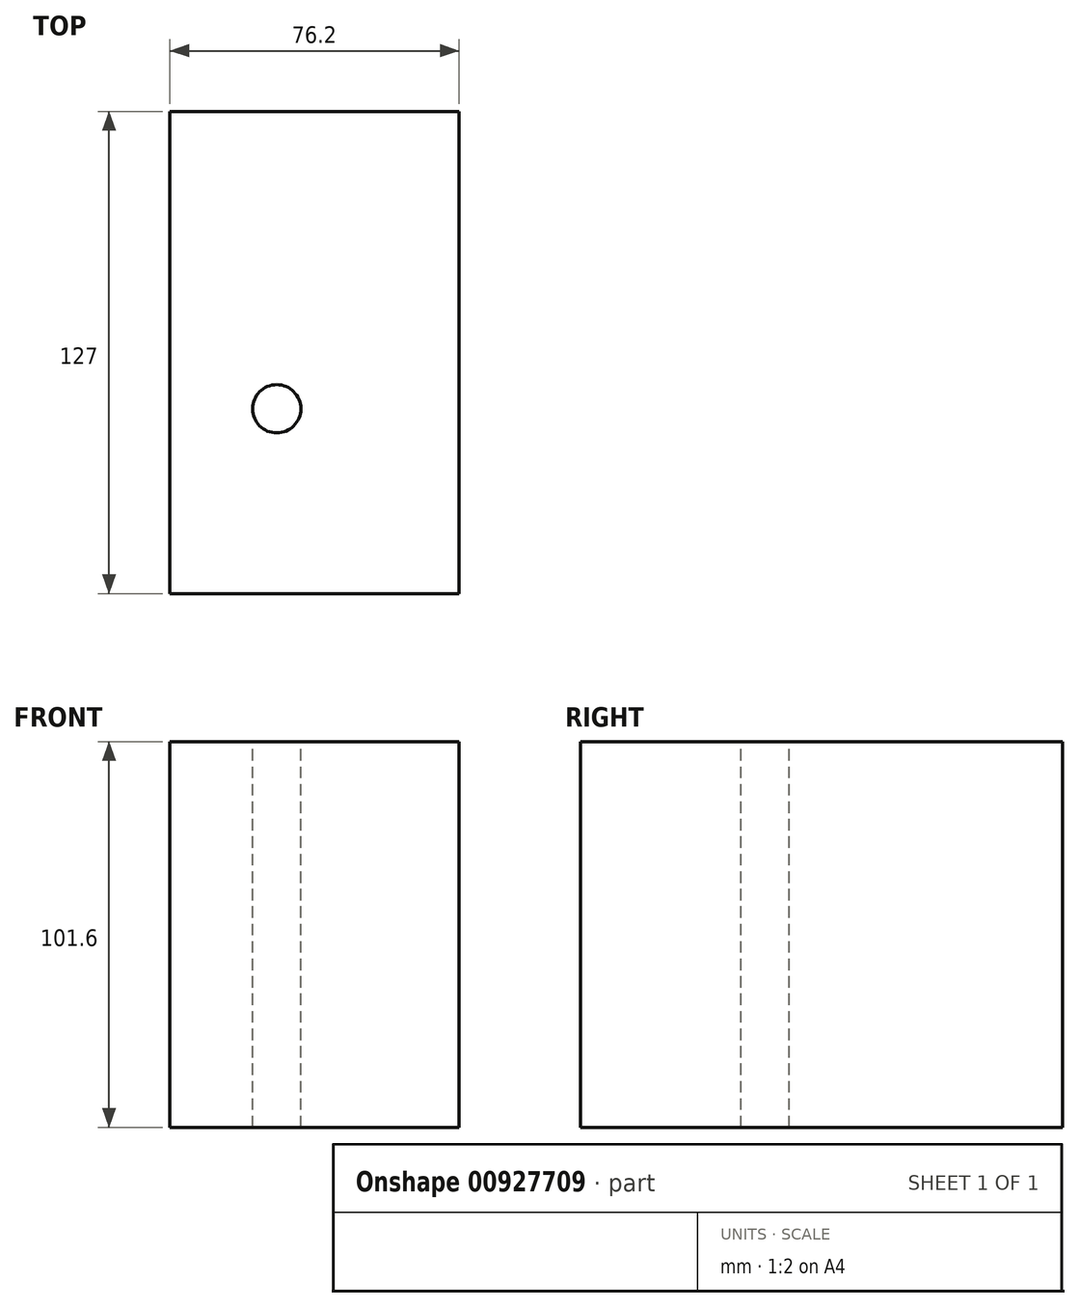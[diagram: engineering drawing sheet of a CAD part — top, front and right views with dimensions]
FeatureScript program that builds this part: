
annotation { "Feature Type Name" : "Feature", "Feature Type Description" : "" }
export const myFeature = defineFeature(function(context is Context, id is Id, definition is map)
    precondition{}
    {
        {
            var Q0;
            Q0=qCreatedBy(makeId("Right.planeOp"),FACE);
            var sketch = newSketch(context, id + "F0", { "sketchPlane" : qUnion([Q0])});
            skLineSegment(sketch, "E0.bottom", {"start": v(-59.91, 50.8) * mm, "end": v(67.09, 50.8) * mm});
            skLineSegment(sketch, "E0.top", {"start": v(-59.91, -50.8) * mm, "end": v(67.09, -50.8) * mm});
            skLineSegment(sketch, "E0.left", {"start": v(-59.91, 50.8) * mm, "end": v(-59.91, -50.8) * mm});
            skLineSegment(sketch, "E0.right", {"start": v(67.09, 50.8) * mm, "end": v(67.09, -50.8) * mm});
            skSolve(sketch);
        }
        {
            var Q0;
            Q0=makeQuery(id+"F0.imprint","IMPRINT",FACE,{"disambiguationData":[TD([[makeQuery(id+"F0.imprint","IMPRINT",EDGE,{"derivedFrom":sQuery(id+"F0.wireOp",EDGE,"E0.bottom")}),-1.0]])]});
            extrude(context, id + "F1", {"entities" : qUnion([Q0]), "depth" : 76.2 * mm, "offsetDistance" : 25.4 * mm});
        }
        {
            var Q0;
            Q0=makeQuery(id+"F1.opExtrude","SWEPT_FACE",FACE,{"disambiguationData":[OSD([sQuery(id+"F0.wireOp",EDGE,"E0.bottom")])]});
            var sketch = newSketch(context, id + "F2", { "sketchPlane" : qUnion([Q0])});
            skLineSegment(sketch, "E1", {"start": v(28.14, -11.26) * mm, "end": v(44.58, 39.2) * mm});
            skSolve(sketch);
        }
        {
            var Q0;
            Q0=sQuery(id+"F2.wireOp",VERTEX,"E1.start");
            var Q1;
            Q1=makeQuery(id+"F1.opExtrude","SWEPT_BODY",BODY,{"disambiguationData":[OSD([sQuery(id+"F0.wireOp",EDGE,"E0.bottom"),sQuery(id+"F0.wireOp",EDGE,"E0.top"),sQuery(id+"F0.wireOp",EDGE,"E0.left"),sQuery(id+"F0.wireOp",EDGE,"E0.right")])]});
            hole(context, id + "F3", {"style" : HoleStyle.C_BORE, "endStyle" : HoleEndStyle.THROUGH, "holeDiameter" : 12.7 * mm, "cBoreDiameter" : 12.7 * mm, "cBoreDepth" : 6.35 * mm, "majorDiameter" : 6.35 * mm, "isTappedThrough" : true, "tappedDepth" : 12.7 * mm, "tapClearance" : 3, "locations" : qUnion([Q0]), "scope" : qUnion([Q1])});
        }
    });
